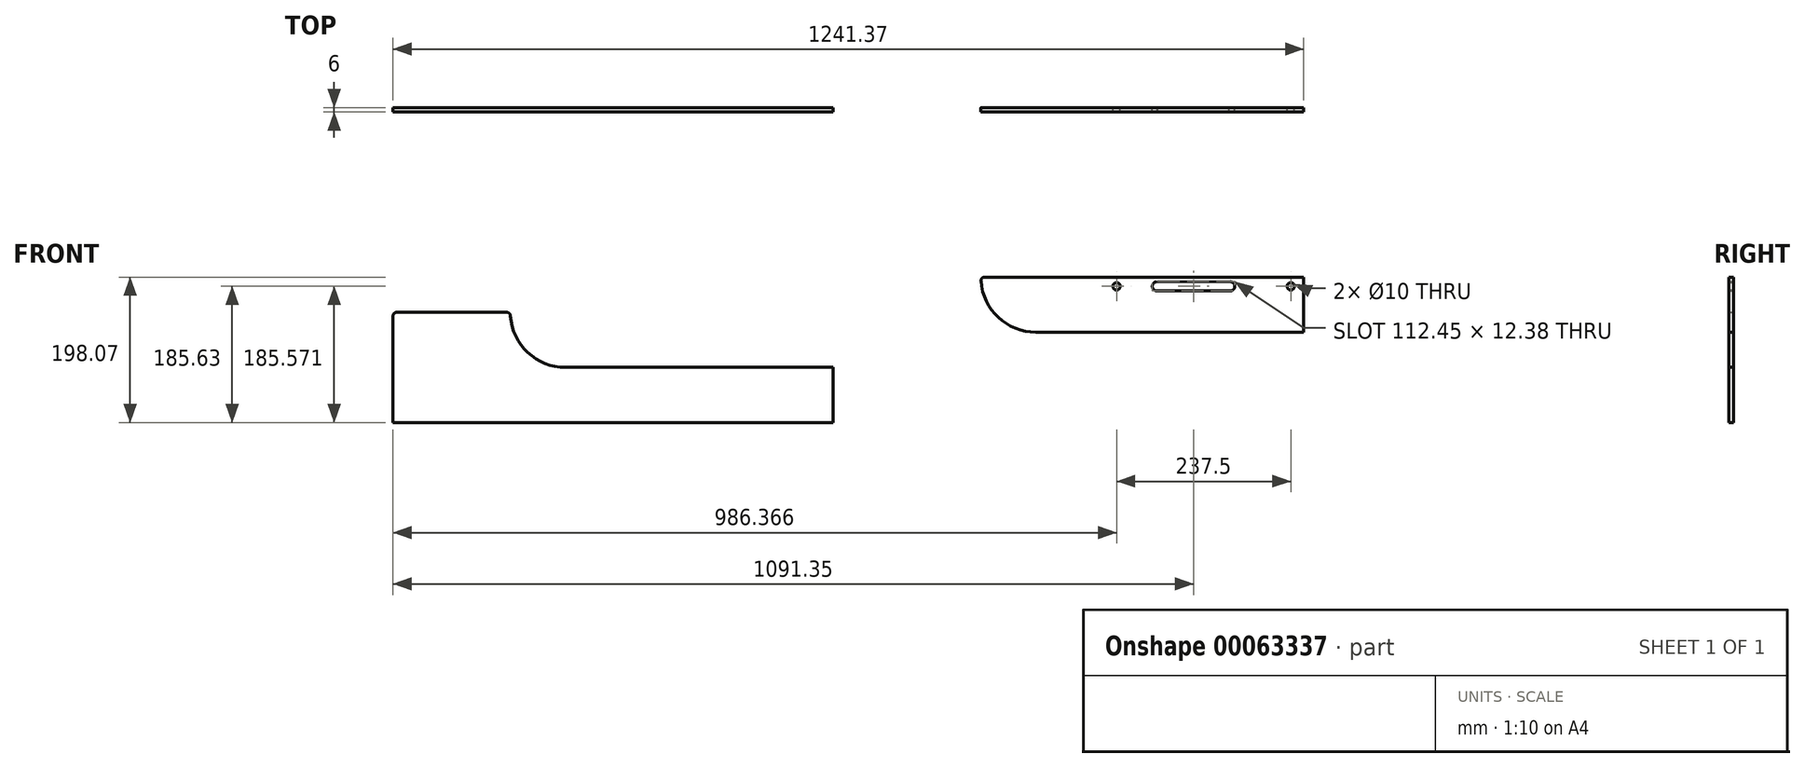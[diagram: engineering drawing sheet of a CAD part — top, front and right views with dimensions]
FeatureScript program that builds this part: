
annotation { "Feature Type Name" : "Feature", "Feature Type Description" : "" }
export const myFeature = defineFeature(function(context is Context, id is Id, definition is map)
    precondition{}
    {
        {
            var Q0;
            Q0=qCreatedBy(makeId("Front.planeOp"),FACE);
            var sketch = newSketch(context, id + "F0", { "sketchPlane" : qUnion([Q0])});
            skLineSegment(sketch, "E0.left", {"start": v(320.53, 271.75) * mm, "end": v(320.53, 271.75) * mm});
            skLineSegment(sketch, "E0.top", {"start": v(245.53, 196.75) * mm, "end": v(-44.47, 196.75) * mm});
            skPoint(sketch, "E1.rect.middle", {"position": v(20.53, 196.75) * mm});
            skLineSegment(sketch, "E0.bottom", {"start": v(320.53, 271.75) * mm, "end": v(-119.47, 271.75) * mm});
            skLineSegment(sketch, "E0.right", {"start": v(-119.47, 271.75) * mm, "end": v(-119.47, 271.75) * mm});
            skArc(sketch, "E2.filletArc", {"start": v(-119.28, 266.4) * mm, "mid": v(-95.58, 216.86) * mm, "end": v(-44.47, 196.75) * mm});
            skLineSegment(sketch, "E1.rect.bottom", {"start": v(-114.3, 271.75) * mm, "end": v(320.53, 271.75) * mm});
            skPoint(sketch, "E2.visualSharp", {"position": v(-119.47, 196.75) * mm});
            skPoint(sketch, "E3.visualSharp", {"position": v(320.53, 196.75) * mm});
            skCircle(sketch, "E4", {"center": v(65.53, 259.25) * mm, "radius": 5 * mm});
            skCircle(sketch, "E5", {"center": v(303.03, 259.25) * mm, "radius": 5 * mm});
            skPoint(sketch, "E6.orphan", {"position": v(-279.47, 271.75) * mm});
            skLineSegment(sketch, "E7.left", {"start": v(-320.84, 223.68) * mm, "end": v(-320.84, 223.68) * mm});
            skLineSegment(sketch, "E8.rect.top", {"start": v(-920.84, 73.68) * mm, "end": v(-320.84, 73.68) * mm});
            skLineSegment(sketch, "E7.top", {"start": v(-395.84, 148.68) * mm, "end": v(-685.84, 148.68) * mm});
            skPoint(sketch, "E8.rect.middle", {"position": v(-620.84, 148.68) * mm});
            skLineSegment(sketch, "E7.bottom", {"start": v(-320.84, 223.68) * mm, "end": v(-760.84, 223.68) * mm});
            skLineSegment(sketch, "E7.right", {"start": v(-760.84, 223.68) * mm, "end": v(-760.84, 223.68) * mm});
            skArc(sketch, "E9.filletArc", {"start": v(-760.7, 219) * mm, "mid": v(-737.19, 169.02) * mm, "end": v(-685.84, 148.68) * mm});
            skLineSegment(sketch, "E8.rect.bottom", {"start": v(-915.84, 223.68) * mm, "end": v(-765.68, 223.68) * mm});
            skLineSegment(sketch, "E8.rect.left", {"start": v(-920.84, 218.68) * mm, "end": v(-920.84, 73.68) * mm});
            skPoint(sketch, "E9.visualSharp", {"position": v(-760.84, 148.68) * mm});
            skPoint(sketch, "E10.visualSharp", {"position": v(-320.84, 148.68) * mm});
            skLineSegment(sketch, "E8.rect.right", {"start": v(-320.84, 223.68) * mm, "end": v(-320.84, 73.68) * mm});
            skCircle(sketch, "E11", {"center": v(-570.84, 211.18) * mm, "radius": 5 * mm});
            skCircle(sketch, "E12", {"center": v(-333.34, 211.18) * mm, "radius": 5 * mm});
            skLineSegment(sketch, "E13.trimOffspring", {"start": v(-685.84, 223.68) * mm, "end": v(-320.84, 223.68) * mm});
            skLineSegment(sketch, "E14", {"start": v(-395.84, 148.68) * mm, "end": v(-320.84, 148.68) * mm});
            skLineSegment(sketch, "E15", {"start": v(320.53, 271.75) * mm, "end": v(320.53, 196.75) * mm});
            skLineSegment(sketch, "E16", {"start": v(320.53, 196.75) * mm, "end": v(245.53, 196.75) * mm});
            skCircle(sketch, "E17", {"center": v(120.53, 259.25) * mm, "radius": 6.25 * mm});
            skCircle(sketch, "E18", {"center": v(220.53, 259.25) * mm, "radius": 6.25 * mm});
            skLineSegment(sketch, "E19", {"start": v(119.87, 265.47) * mm, "end": v(220.52, 265.5) * mm});
            skLineSegment(sketch, "E20", {"start": v(221.92, 253.16) * mm, "end": v(121.92, 253.16) * mm});
            skPoint(sketch, "E21.visualSharp", {"position": v(-119.47, 271.75) * mm});
            skArc(sketch, "E21.filletArc", {"start": v(-114.3, 271.75) * mm, "mid": v(-117.95, 270.16) * mm, "end": v(-119.28, 266.4) * mm});
            skPoint(sketch, "E22.visualSharp", {"position": v(-760.84, 223.68) * mm});
            skArc(sketch, "E22.filletArc", {"start": v(-760.7, 219) * mm, "mid": v(-762.26, 222.33) * mm, "end": v(-765.68, 223.68) * mm});
            skPoint(sketch, "E23.visualSharp", {"position": v(-920.84, 223.68) * mm});
            skArc(sketch, "E23.filletArc", {"start": v(-915.84, 223.68) * mm, "mid": v(-919.37, 222.22) * mm, "end": v(-920.84, 218.68) * mm});
            skSolve(sketch);
        }
        {
            var Q0;
            Q0=makeQuery(id+"F0.imprint","IMPRINT",FACE,{"disambiguationData":[TD([[makeQuery(id+"F0.imprint","IMPRINT",EDGE,{"derivedFrom":sQuery(id+"F0.wireOp",EDGE,"E8.rect.top")}),1.0]])]});
            var Q1;
            Q1=makeQuery(id+"F0.imprint","IMPRINT",FACE,{"disambiguationData":[TD([[makeQuery(id+"F0.imprint","IMPRINT",EDGE,{"derivedFrom":sQuery(id+"F0.wireOp",EDGE,"E0.top")}),-1.0]])]});
            extrude(context, id + "F1", {"entities" : qUnion([Q0, Q1]), "depth" : 6 * mm});
        }
    });
